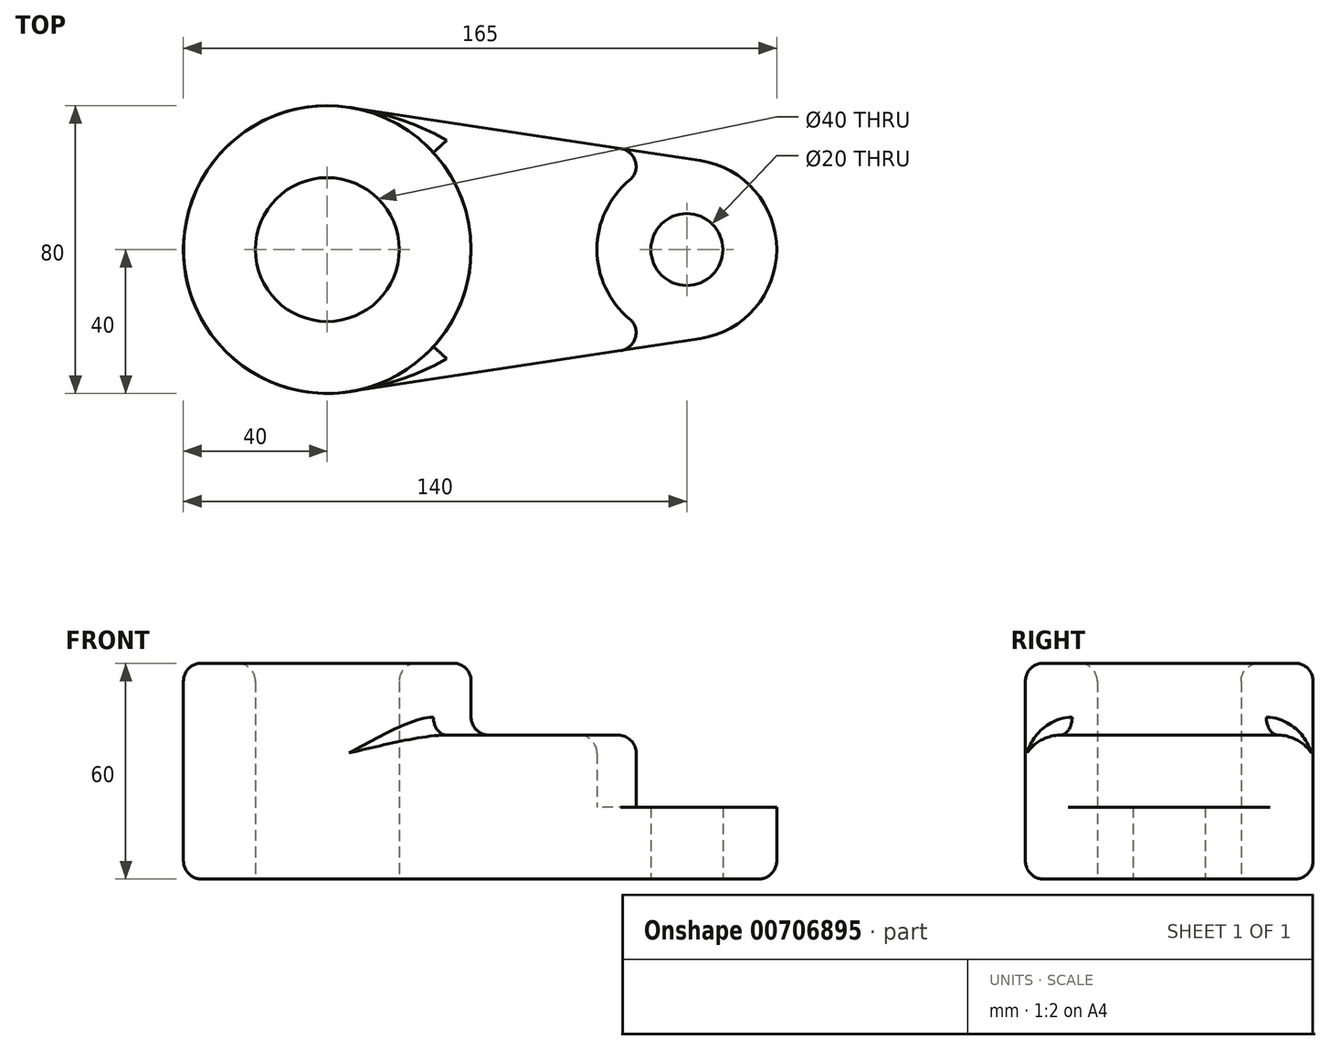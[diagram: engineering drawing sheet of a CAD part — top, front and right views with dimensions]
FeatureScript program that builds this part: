
annotation { "Feature Type Name" : "Feature", "Feature Type Description" : "" }
export const myFeature = defineFeature(function(context is Context, id is Id, definition is map)
    precondition{}
    {
        {
            var Q0;
            Q0=qCreatedBy(makeId("Top.planeOp"),FACE);
            var sketch = newSketch(context, id + "F0", { "sketchPlane" : qUnion([Q0])});
            skCircle(sketch, "E0", {"center": v(-50, 0) * mm, "radius": 20 * mm});
            skCircle(sketch, "E1", {"center": v(-50, 0) * mm, "radius": 40 * mm});
            skCircle(sketch, "E2", {"center": v(50, 0) * mm, "radius": 25 * mm});
            skCircle(sketch, "E3", {"center": v(50, 0) * mm, "radius": 10 * mm});
            skLineSegment(sketch, "E4", {"start": v(-44, 39.55) * mm, "end": v(53.75, 24.72) * mm});
            skLineSegment(sketch, "E5", {"start": v(-44, -39.55) * mm, "end": v(53.75, -24.72) * mm});
            skSolve(sketch);
        }
        {
            var Q0;
            Q0=makeQuery(id+"F0.imprint","IMPRINT",FACE,{"disambiguationData":[TD([[makeQuery(id+"F0.imprint","IMPRINT",EDGE,{"derivedFrom":sQuery(id+"F0.wireOp",EDGE,"E0")}),-1.0]])]});
            extrude(context, id + "F1", {"entities" : qUnion([Q0]), "depth" : 60 * mm, "offsetDistance" : 25 * mm});
        }
        {
            var Q0;
            {var subQ0=sQuery(id+"F0.wireOp",EDGE,"E4");Q0=makeQuery(id+"F0.imprint","IMPRINT",FACE,{"disambiguationData":[TD([[makeQuery(id+"F0.imprint","IMPRINT",EDGE,{"derivedFrom":subQ0}),-1.0]])]});}
            extrude(context, id + "F2", {"entities" : qUnion([Q0]), "operationType" : NewBodyOperationType.ADD, "depth" : 40 * mm, "offsetDistance" : 25 * mm});
        }
        {
            var Q0;
            Q0=makeQuery(id+"F0.imprint","IMPRINT",FACE,{"disambiguationData":[TD([[makeQuery(id+"F0.imprint","IMPRINT",EDGE,{"derivedFrom":sQuery(id+"F0.wireOp",EDGE,"E3")}),-1.0]])]});
            extrude(context, id + "F3", {"entities" : qUnion([Q0]), "operationType" : NewBodyOperationType.ADD, "depth" : 20 * mm, "offsetDistance" : 25 * mm});
        }
        {
            var Q0;
            Q0=makeQuery(id+"F1.opExtrude","CAP_FACE",FACE,{"disambiguationData":[OSD([sQuery(id+"F0.wireOp",EDGE,"E0"),sQuery(id+"F0.wireOp",EDGE,"E1")])],"isStart":false});
            fillet(context, id + "F4", {"entities" : qUnion([Q0]), "radius" : 5 * mm, "tangentPropagation" : true, "allowEdgeOverflow" : false});
        }
        {
            var Q0;
            Q0=makeQuery(id+"F2.opExtrude","SWEPT_FACE",FACE,{"disambiguationData":[OSD([sQuery(id+"F0.wireOp",EDGE,"E5")])]});
            var Q1;
            Q1=makeQuery(id+"F2.opExtrude","SWEPT_FACE",FACE,{"disambiguationData":[OSD([sQuery(id+"F0.wireOp",EDGE,"E4")])]});
            var Q2;
            Q2=makeQuery(id+"F2.opExtrude","CAP_FACE",FACE,{"disambiguationData":[OSD([sQuery(id+"F0.wireOp",EDGE,"E1"),sQuery(id+"F0.wireOp",EDGE,"E2"),sQuery(id+"F0.wireOp",EDGE,"E4"),sQuery(id+"F0.wireOp",EDGE,"E5")])],"isStart":false});
            fillet(context, id + "F5", {"entities" : qUnion([Q0, Q1, Q2]), "radius" : 5 * mm, "tangentPropagation" : true, "allowEdgeOverflow" : false});
        }
    });
